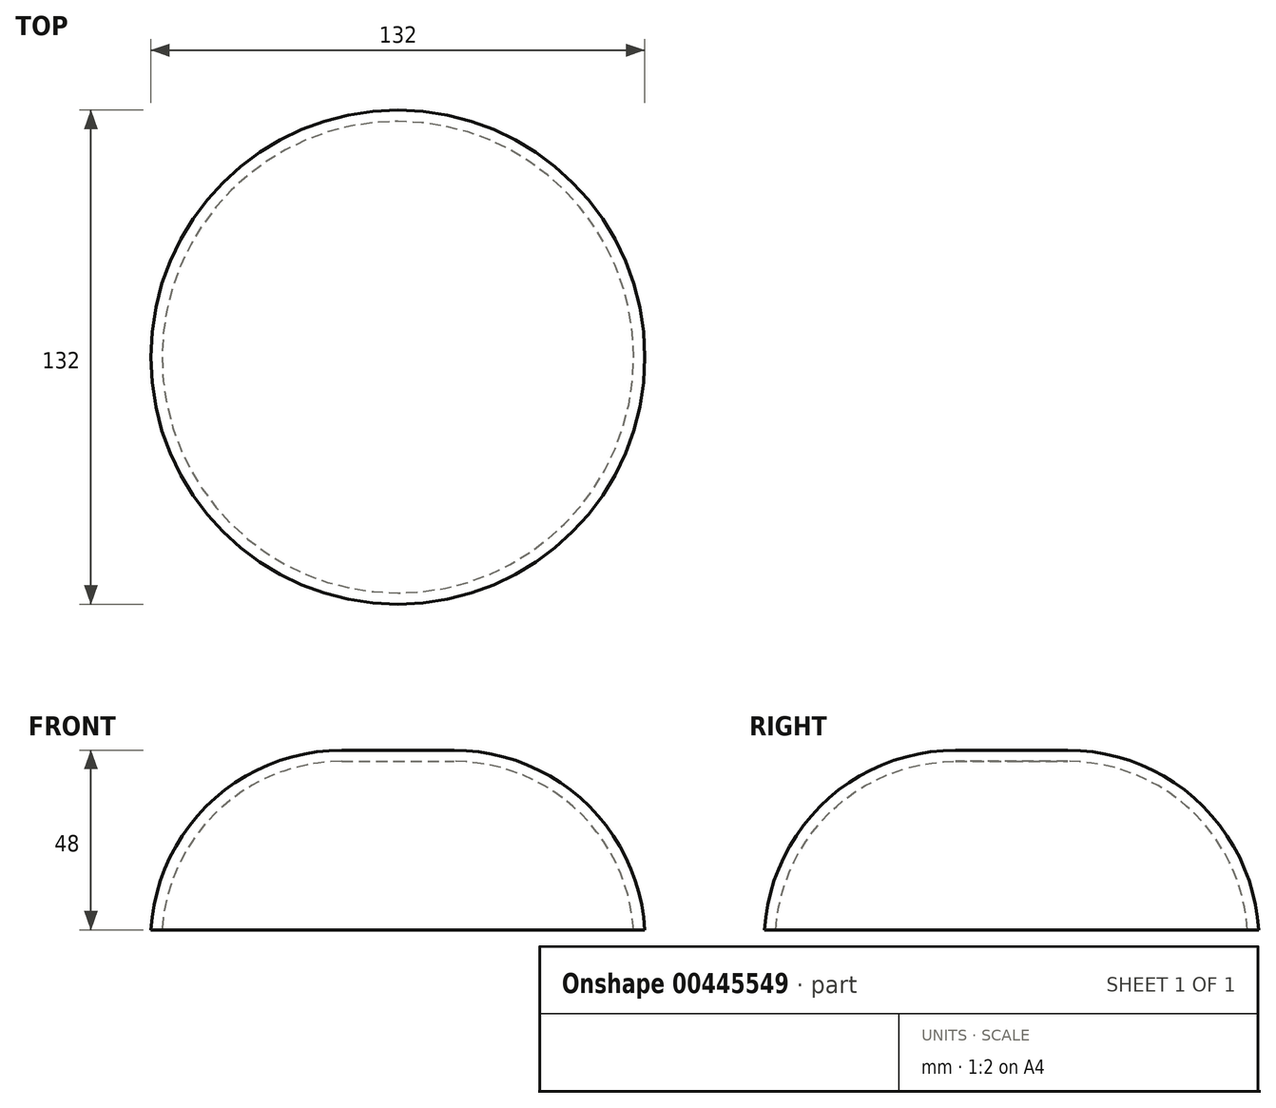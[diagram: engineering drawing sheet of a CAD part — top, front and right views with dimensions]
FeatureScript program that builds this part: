
annotation { "Feature Type Name" : "Feature", "Feature Type Description" : "" }
export const myFeature = defineFeature(function(context is Context, id is Id, definition is map)
    precondition{}
    {
        {
            var Q0;
            Q0=qCreatedBy(makeId("Front.planeOp"),FACE);
            var sketch = newSketch(context, id + "F0", { "sketchPlane" : qUnion([Q0])});
            skLineSegment(sketch, "E0", {"start": v(0, 45) * mm, "end": v(15, 45) * mm});
            skArc(sketch, "E1", {"start": v(15, 45) * mm, "mid": v(47.9, 32) * mm, "end": v(63, 0) * mm});
            skLineSegment(sketch, "E2", {"start": v(0, 45) * mm, "end": v(0, 48) * mm});
            skLineSegment(sketch, "E3", {"start": v(0, 48) * mm, "end": v(15, 48) * mm});
            skLineSegment(sketch, "E4", {"start": v(63, 0) * mm, "end": v(66, 0) * mm});
            skArc(sketch, "E5", {"start": v(15, 48) * mm, "mid": v(50.02, 34.11) * mm, "end": v(66, 0) * mm});
            skSolve(sketch);
        }
        {
            var Q0;
            Q0 = qSketchRegion(id + "F0", true);
            var Q1;
            Q1=sQuery(id+"F0.wireOp",EDGE,"E2");
            revolve(context, id + "F1", {"entities" : qUnion([Q0]), "axis" : qUnion([Q1]), "revolveType" : RevolveType.FULL});
        }
    });
